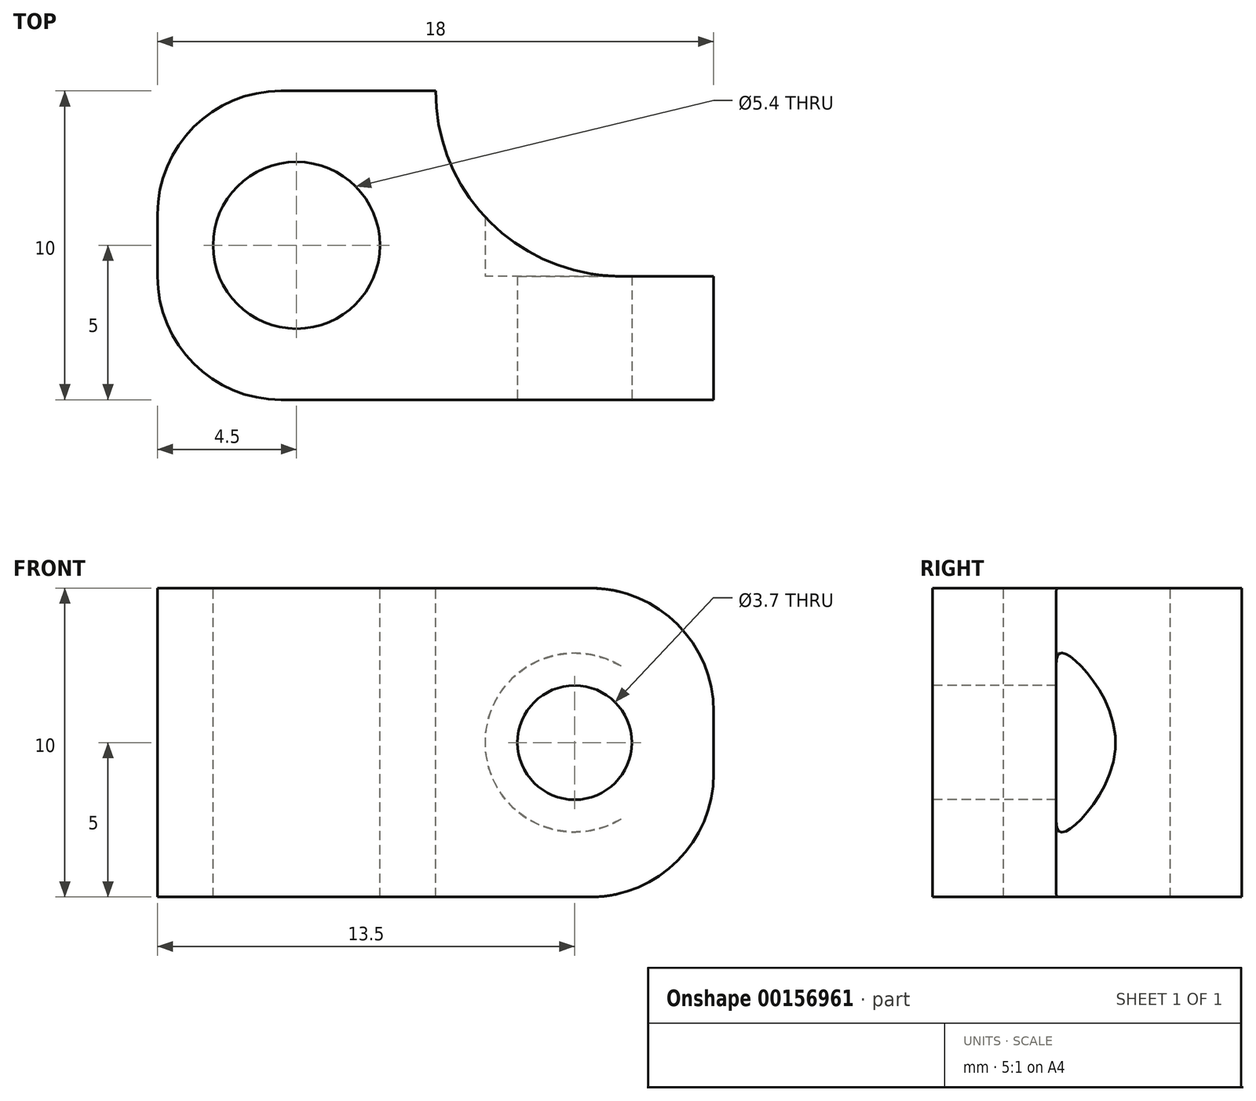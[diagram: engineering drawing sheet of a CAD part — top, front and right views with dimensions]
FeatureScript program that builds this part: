
annotation { "Feature Type Name" : "Feature", "Feature Type Description" : "" }
export const myFeature = defineFeature(function(context is Context, id is Id, definition is map)
    precondition{}
    {
        {
            var Q0;
            Q0=qCreatedBy(makeId("Top.planeOp"),FACE);
            var sketch = newSketch(context, id + "F0", { "sketchPlane" : qUnion([Q0])});
            skLineSegment(sketch, "E0.bottom", {"start": v(9, 5) * mm, "end": v(-9, 5) * mm});
            skLineSegment(sketch, "E0.top", {"start": v(9, -5) * mm, "end": v(-9, -5) * mm});
            skLineSegment(sketch, "E0.left", {"start": v(9, 5) * mm, "end": v(9, -5) * mm});
            skLineSegment(sketch, "E0.right", {"start": v(-9, 5) * mm, "end": v(-9, -5) * mm});
            skPoint(sketch, "E0.middle", {"position": v(0, 0) * mm});
            skSolve(sketch);
        }
        {
            var Q0;
            Q0 = qSketchRegion(id + "F0", true);
            extrude(context, id + "F1", {"entities" : qUnion([Q0]), "depth" : 10 * mm});
        }
        {
            var Q0;
            Q0=makeQuery(id+"F1.opExtrude","CAP_FACE",FACE,{"disambiguationData":[OSD([sQuery(id+"F0.wireOp",EDGE,"E0.bottom"),sQuery(id+"F0.wireOp",EDGE,"E0.top"),sQuery(id+"F0.wireOp",EDGE,"E0.left"),sQuery(id+"F0.wireOp",EDGE,"E0.right")])],"isStart":false});
            var sketch = newSketch(context, id + "F2", { "sketchPlane" : qUnion([Q0])});
            skCircle(sketch, "E1", {"center": v(-4.5, 0) * mm, "radius": 2.7 * mm});
            skSolve(sketch);
        }
        {
            var Q0;
            Q0 = qSketchRegion(id + "F2", true);
            extrude(context, id + "F3", {"entities" : qUnion([Q0]), "operationType" : NewBodyOperationType.REMOVE, "oppositeDirection" : true, "depth" : 25 * mm});
        }
        {
            var Q0;
            Q0=makeQuery(id+"F1.opExtrude","SWEPT_FACE",FACE,{"disambiguationData":[OSD([sQuery(id+"F0.wireOp",EDGE,"E0.top")])]});
            var sketch = newSketch(context, id + "F4", { "sketchPlane" : qUnion([Q0])});
            skCircle(sketch, "E2", {"center": v(4.5, 5) * mm, "radius": 1.85 * mm});
            skPoint(sketch, "E3", {"position": v(9, 5) * mm});
            skPoint(sketch, "E4", {"position": v(0, 10) * mm});
            skPoint(sketch, "E5", {"position": v(4.5, 10) * mm});
            skPoint(sketch, "E6", {"position": v(9, 10) * mm});
            skSolve(sketch);
        }
        {
            var Q0;
            Q0 = qSketchRegion(id + "F4", true);
            extrude(context, id + "F5", {"entities" : qUnion([Q0]), "operationType" : NewBodyOperationType.REMOVE, "oppositeDirection" : true, "depth" : 25 * mm});
        }
        {
            var Q0;
            Q0=makeQuery(id+"F1.opExtrude","CAP_EDGE",EDGE,{"disambiguationData":[OSD([sQuery(id+"F0.wireOp",EDGE,"E0.left")])],"isStart":false});
            var Q1;
            Q1=makeQuery(id+"F1.opExtrude","CAP_EDGE",EDGE,{"disambiguationData":[OSD([sQuery(id+"F0.wireOp",EDGE,"E0.left")])],"isStart":true});
            var Q2;
            Q2=makeQuery(id+"F1.opExtrude","SWEPT_EDGE",EDGE,{"disambiguationData":[OSD([sQuery(id+"F0.wireOp",EDGE,"E0.top"),sQuery(id+"F0.wireOp",EDGE,"E0.right")])]});
            var Q3;
            Q3=makeQuery(id+"F1.opExtrude","SWEPT_EDGE",EDGE,{"disambiguationData":[OSD([sQuery(id+"F0.wireOp",EDGE,"E0.bottom"),sQuery(id+"F0.wireOp",EDGE,"E0.right")])]});
            fillet(context, id + "F6", {"entities" : qUnion([Q0, Q1, Q2, Q3]), "radius" : 4 * mm, "tangentPropagation" : true, "allowEdgeOverflow" : false});
        }
        {
            var Q0;
            Q0=makeQuery(id+"F1.opExtrude","CAP_FACE",FACE,{"disambiguationData":[OSD([sQuery(id+"F0.wireOp",EDGE,"E0.bottom"),sQuery(id+"F0.wireOp",EDGE,"E0.top"),sQuery(id+"F0.wireOp",EDGE,"E0.left"),sQuery(id+"F0.wireOp",EDGE,"E0.right")])],"isStart":false});
            var sketch = newSketch(context, id + "F7", { "sketchPlane" : qUnion([Q0])});
            skLineSegment(sketch, "E7.bottom", {"start": v(0, 5) * mm, "end": v(10.19, 5) * mm});
            skLineSegment(sketch, "E7.top", {"start": v(0, -1) * mm, "end": v(10.19, -1) * mm});
            skLineSegment(sketch, "E7.left", {"start": v(0, 5) * mm, "end": v(0, -1) * mm});
            skLineSegment(sketch, "E7.right", {"start": v(10.19, 5) * mm, "end": v(10.19, -1) * mm});
            skSolve(sketch);
        }
        {
            var Q0;
            Q0 = qSketchRegion(id + "F7", true);
            extrude(context, id + "F8", {"entities" : qUnion([Q0]), "operationType" : NewBodyOperationType.REMOVE, "oppositeDirection" : true, "depth" : 25 * mm});
        }
        {
            var Q0;
            Q0=makeQuery(id+"F8.boolean.opBoolean","COPY",EDGE,{"derivedFrom":makeQuery(id+"F8.opExtrude","SWEPT_EDGE",EDGE,{"disambiguationData":[OSD([sQuery(id+"F7.wireOp",EDGE,"E7.top"),sQuery(id+"F7.wireOp",EDGE,"E7.left")])]})});
            fillet(context, id + "F9", {"entities" : qUnion([Q0]), "radius" : 6 * mm, "tangentPropagation" : true, "allowEdgeOverflow" : false});
        }
        {
            var Q0;
            Q0=makeQuery(id+"F8.boolean.opBoolean","COPY",FACE,{"derivedFrom":makeQuery(id+"F8.opExtrude","SWEPT_FACE",FACE,{"disambiguationData":[OSD([sQuery(id+"F7.wireOp",EDGE,"E7.top")])]})});
            var sketch = newSketch(context, id + "F10", { "sketchPlane" : qUnion([Q0])});
            skCircle(sketch, "E8", {"center": v(-4.5, 5) * mm, "radius": 2.9 * mm});
            skSolve(sketch);
        }
        {
            var Q0;
            Q0 = qSketchRegion(id + "F10", true);
            extrude(context, id + "F11", {"entities" : qUnion([Q0]), "operationType" : NewBodyOperationType.REMOVE, "depth" : 25 * mm});
        }
    });
